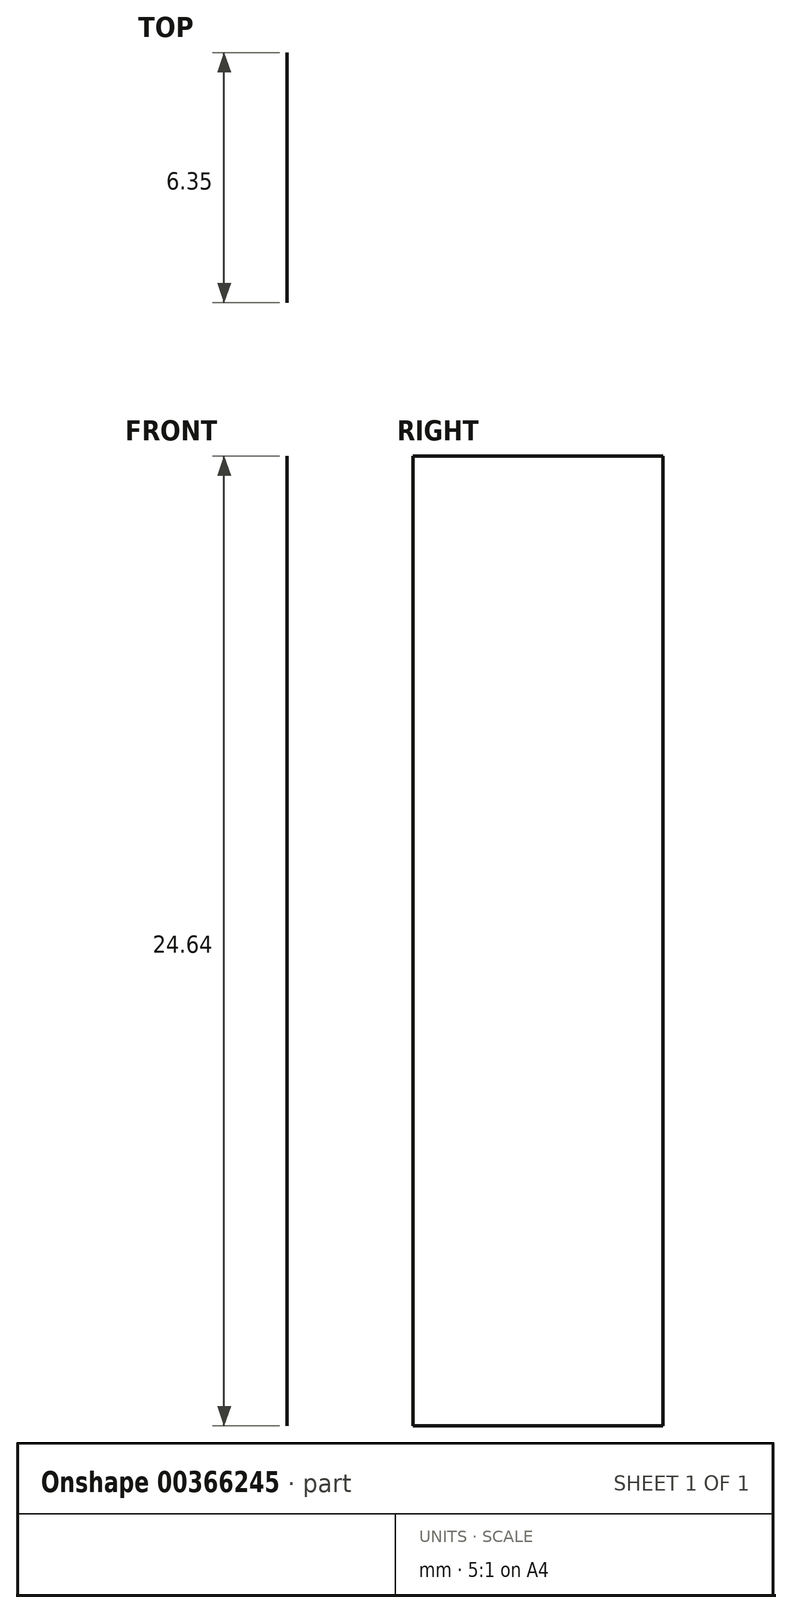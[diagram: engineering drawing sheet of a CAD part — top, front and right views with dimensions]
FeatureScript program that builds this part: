
annotation { "Feature Type Name" : "Feature", "Feature Type Description" : "" }
export const myFeature = defineFeature(function(context is Context, id is Id, definition is map)
    precondition{}
    {
        {
            var Q0;
            Q0=qCreatedBy(makeId("Front.planeOp"),FACE);
            var sketch = newSketch(context, id + "F0", { "sketchPlane" : qUnion([Q0])});
            skLineSegment(sketch, "E0", {"start": v(0, 0) * mm, "end": v(0, 12.7) * mm});
            skLineSegment(sketch, "E1", {"start": v(0, 12.7) * mm, "end": v(10.16, 12.7) * mm});
            skLineSegment(sketch, "E2", {"start": v(10.16, 12.7) * mm, "end": v(10.16, 10.16) * mm});
            skLineSegment(sketch, "E3", {"start": v(10.16, 10.16) * mm, "end": v(56.13, 10.16) * mm});
            skLineSegment(sketch, "E4", {"start": v(56.13, 10.16) * mm, "end": v(56.13, 12.7) * mm});
            skLineSegment(sketch, "E5", {"start": v(56.13, 12.7) * mm, "end": v(66.3, 12.7) * mm});
            skLineSegment(sketch, "E6", {"start": v(66.3, 12.7) * mm, "end": v(66.3, 0) * mm});
            skLineSegment(sketch, "E7", {"start": v(66.3, 0) * mm, "end": v(0, 0) * mm});
            skLineSegment(sketch, "E8", {"start": v(5.84, 15.24) * mm, "end": v(-0.5, 15.24) * mm});
            skLineSegment(sketch, "E9", {"start": v(-0.5, 15.24) * mm, "end": v(-10.88, 3.85) * mm});
            skLineSegment(sketch, "E10", {"start": v(0, 0) * mm, "end": v(-6.65, 0) * mm});
            skCircle(sketch, "E11", {"center": v(-6.65, 0) * mm, "radius": 5.72 * mm});
            skCircle(sketch, "E12", {"center": v(-6.65, 0) * mm, "radius": 3.18 * mm});
            skLineSegment(sketch, "E13", {"start": v(5.84, 15.24) * mm, "end": v(5.84, -9.4) * mm});
            skLineSegment(sketch, "E14", {"start": v(5.84, -9.4) * mm, "end": v(-8.18, -5.5) * mm});
            skSolve(sketch);
        }
        {
            var Q0;
            Q0=sQuery(id+"F0.wireOp",EDGE,"E13");
            extrude(context, id + "F1", {"bodyType" : ToolBodyType.SURFACE, "surfaceEntities" : qUnion([Q0]), "depth" : 6.35 * mm});
        }
    });
